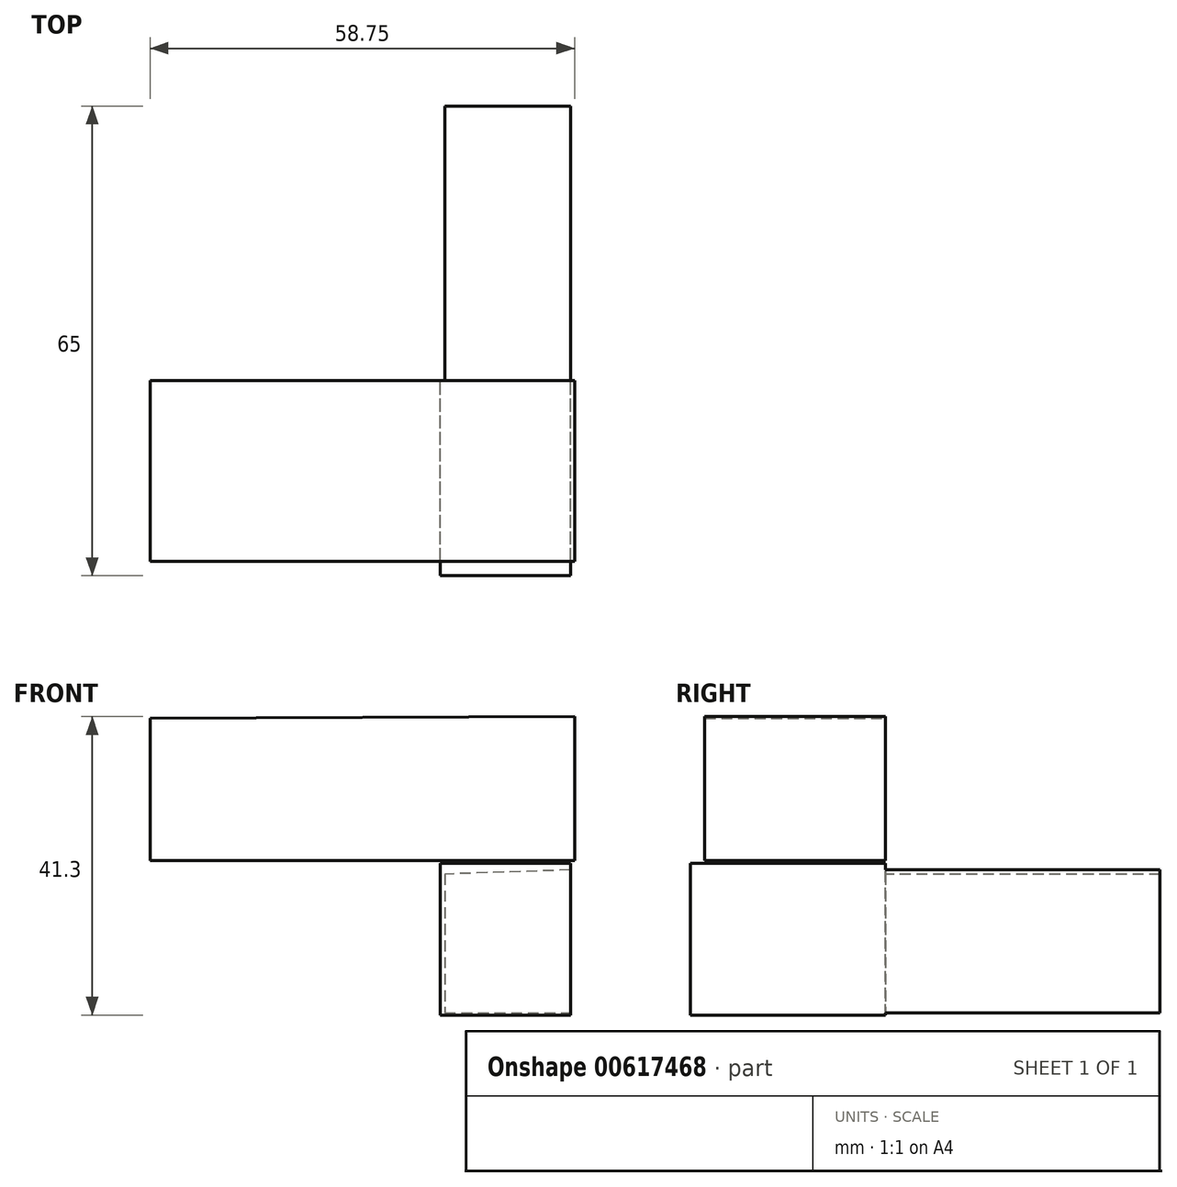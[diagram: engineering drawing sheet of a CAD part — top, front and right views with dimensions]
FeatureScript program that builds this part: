
annotation { "Feature Type Name" : "Feature", "Feature Type Description" : "" }
export const myFeature = defineFeature(function(context is Context, id is Id, definition is map)
    precondition{}
    {
        {
            var Q0;
            Q0=qCreatedBy(makeId("Front.planeOp"),FACE);
            var sketch = newSketch(context, id + "F0", { "sketchPlane" : qUnion([Q0])});
            skLineSegment(sketch, "E0", {"start": v(-31.62, 26.64) * mm, "end": v(-31.62, 6.98) * mm});
            skLineSegment(sketch, "E1", {"start": v(-31.62, 6.98) * mm, "end": v(27.13, 6.98) * mm});
            skLineSegment(sketch, "E2", {"start": v(27.13, 6.98) * mm, "end": v(27.13, 26.9) * mm});
            skLineSegment(sketch, "E3", {"start": v(27.13, 26.9) * mm, "end": v(-31.62, 26.64) * mm});
            skSolve(sketch);
        }
        {
            var Q0;
            Q0=makeQuery(id+"F0.imprint","IMPRINT",FACE,{"disambiguationData":[TD([[makeQuery(id+"F0.imprint","IMPRINT",EDGE,{"derivedFrom":sQuery(id+"F0.wireOp",EDGE,"E0")}),1.0]])]});
            extrude(context, id + "F1", {"entities" : qUnion([Q0]), "depth" : 25 * mm, "offsetDistance" : 25 * mm});
        }
        {
            var Q0;
            Q0=qCreatedBy(makeId("Front.planeOp"),FACE);
            var sketch = newSketch(context, id + "F2", { "sketchPlane" : qUnion([Q0])});
            skLineSegment(sketch, "E4", {"start": v(8.55, 6.6) * mm, "end": v(26.55, 6.6) * mm});
            skLineSegment(sketch, "E5", {"start": v(26.55, 6.6) * mm, "end": v(26.55, -14.4) * mm});
            skLineSegment(sketch, "E6", {"start": v(26.55, -14.4) * mm, "end": v(8.55, -14.4) * mm});
            skLineSegment(sketch, "E7", {"start": v(8.55, -14.4) * mm, "end": v(8.55, 6.6) * mm});
            skSolve(sketch);
        }
        {
            var Q0;
            Q0 = qSketchRegion(id + "F2", true);
            extrude(context, id + "F3", {"entities" : qUnion([Q0]), "depth" : 27 * mm, "offsetDistance" : 25 * mm});
        }
        {
            var Q0;
            Q0=qCreatedBy(makeId("Front.planeOp"),FACE);
            var sketch = newSketch(context, id + "F4", { "sketchPlane" : qUnion([Q0])});
            skLineSegment(sketch, "E8", {"start": v(9.15, 5.1) * mm, "end": v(9.15, -14.1) * mm});
            skLineSegment(sketch, "E9", {"start": v(8.55, -14.1) * mm, "end": v(26.55, -14.1) * mm});
            skLineSegment(sketch, "E10", {"start": v(26.55, -14.7) * mm, "end": v(26.55, 5.7) * mm});
            skLineSegment(sketch, "E11", {"start": v(27.15, 5.7) * mm, "end": v(9.15, 5.1) * mm});
            skSolve(sketch);
        }
        {
            var Q0;
            Q0 = qSketchRegion(id + "F4", true);
            extrude(context, id + "F5", {"entities" : qUnion([Q0]), "operationType" : NewBodyOperationType.ADD, "oppositeDirection" : true, "depth" : 38 * mm, "offsetDistance" : 25 * mm});
        }
    });
